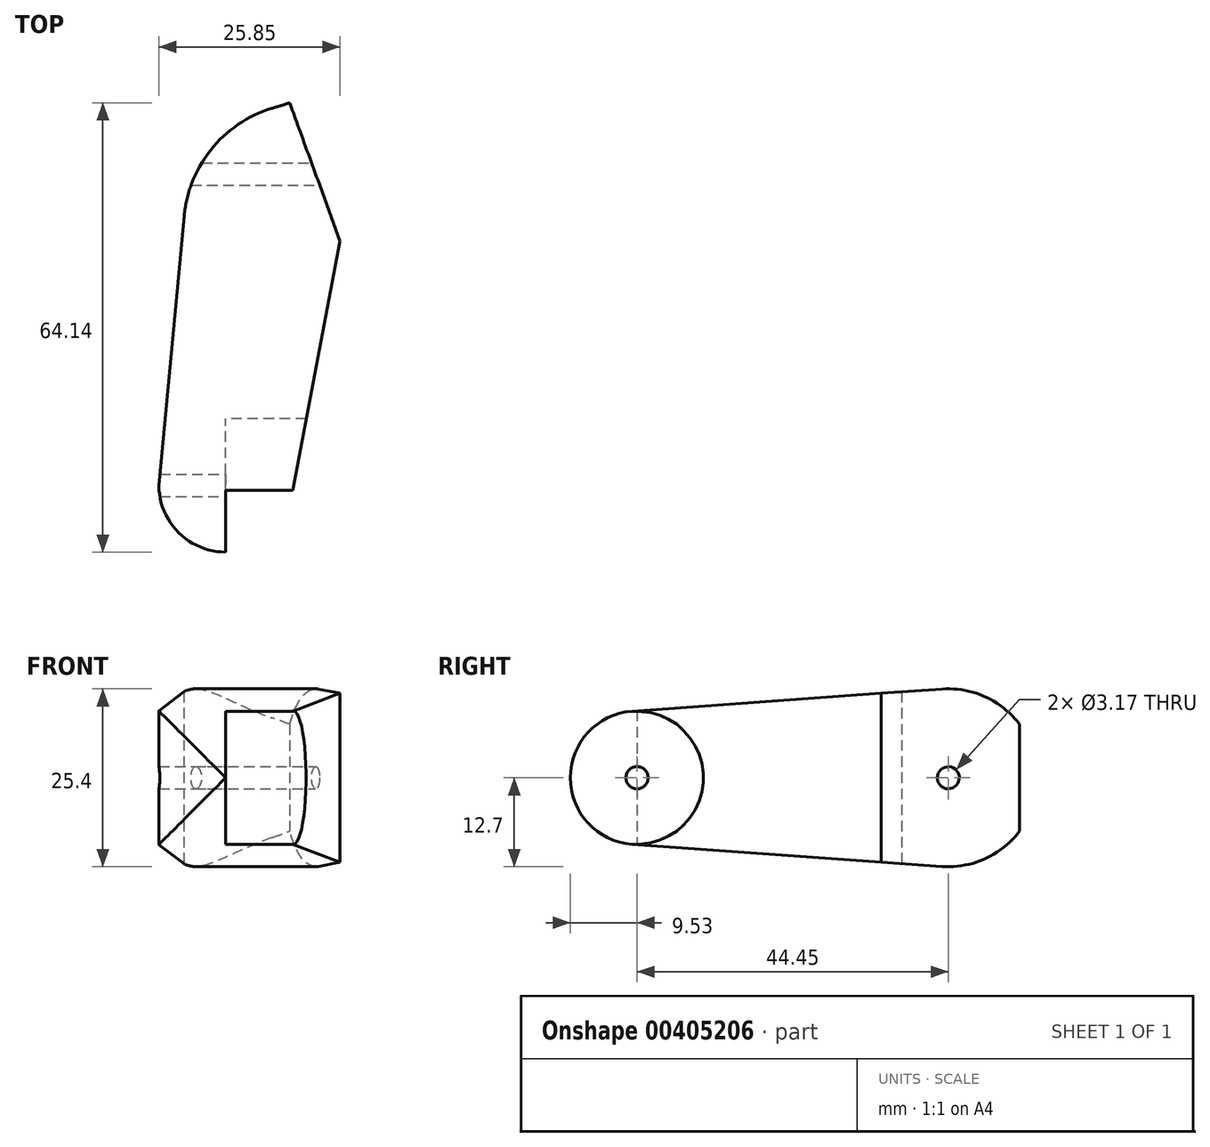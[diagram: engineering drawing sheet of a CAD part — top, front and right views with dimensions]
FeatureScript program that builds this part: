
annotation { "Feature Type Name" : "Feature", "Feature Type Description" : "" }
export const myFeature = defineFeature(function(context is Context, id is Id, definition is map)
    precondition{}
    {
        {
            var Q0;
            Q0=qCreatedBy(makeId("Top.planeOp"),FACE);
            var sketch = newSketch(context, id + "F0", { "sketchPlane" : qUnion([Q0])});
            skLineSegment(sketch, "E0", {"start": v(-24.07, -44.45) * mm, "end": v(33.85, -44.45) * mm, "construction": true});
            skLineSegment(sketch, "E1", {"start": v(-3.18, 19.25) * mm, "end": v(-3.17, -36.51) * mm, "construction": true});
            skLineSegment(sketch, "E2", {"start": v(13.15, -9.58) * mm, "end": v(6.1, -46.62) * mm});
            skPoint(sketch, "E3.middle", {"position": v(-3.17, -44.45) * mm});
            skLineSegment(sketch, "E4", {"start": v(0, 0) * mm, "end": v(-3.17, 0) * mm});
            skLineSegment(sketch, "E5", {"start": v(0, 0) * mm, "end": v(-36.28, 0) * mm});
            skPoint(sketch, "E5.endSnap0", {"position": v(-1.59, 0) * mm});
            skLineSegment(sketch, "E6.0", {"start": v(5.97, 10.16) * mm, "end": v(13.15, -9.58) * mm});
            skLineSegment(sketch, "E7", {"start": v(5.97, 10.16) * mm, "end": v(3.44, 9.4) * mm});
            skPoint(sketch, "E8.visualSharp", {"position": v(12.41, -13.45) * mm});
            skPoint(sketch, "E9.visualSharp", {"position": v(-8.5, 5.77) * mm});
            skArc(sketch, "E9.filletArc", {"start": v(3.44, 9.4) * mm, "mid": v(-5.4, 3.34) * mm, "end": v(-9.14, -6.69) * mm});
            skArc(sketch, "E10", {"start": v(-12.7, -44.45) * mm, "mid": v(-4.27, -53.91) * mm, "end": v(6.1, -46.62) * mm});
            skLineSegment(sketch, "E11", {"start": v(-9.14, -6.69) * mm, "end": v(-12.7, -44.45) * mm});
            skSolve(sketch);
        }
        {
            var Q0;
            Q0=qCreatedBy(makeId("Right.planeOp"),FACE);
            var sketch = newSketch(context, id + "F1", { "sketchPlane" : qUnion([Q0])});
            skArc(sketch, "E12", {"start": v(-0.9, -12.67) * mm, "mid": v(12.7, 0) * mm, "end": v(-0.9, 12.67) * mm});
            skArc(sketch, "E13", {"start": v(-45.13, 9.5) * mm, "mid": v(-53.98, 0) * mm, "end": v(-45.13, -9.5) * mm});
            skCircle(sketch, "E14", {"center": v(0, 0) * mm, "radius": 1.59 * mm});
            skCircle(sketch, "E15", {"center": v(-44.45, 0) * mm, "radius": 1.59 * mm});
            skLineSegment(sketch, "E16", {"start": v(-0.9, 12.67) * mm, "end": v(-45.13, 9.5) * mm});
            skLineSegment(sketch, "E17", {"start": v(-0.9, -12.67) * mm, "end": v(-45.13, -9.5) * mm});
            skSolve(sketch);
        }
        {
            var Q0;
            Q0=makeQuery(id+"F1.imprint","IMPRINT",FACE,{"disambiguationData":[TD([[makeQuery(id+"F1.imprint","IMPRINT",EDGE,{"derivedFrom":sQuery(id+"F1.wireOp",EDGE,"E12")}),1.0]])]});
            extrude(context, id + "F2", {"entities" : qUnion([Q0]), "endBound" : BoundingType.SYMMETRIC, "oppositeDirection" : true, "depth" : 50.8 * mm});
        }
        {
            var Q0;
            Q0=qSketchRegion(id+"F0",true);
            extrude(context, id + "F3", {"entities" : qUnion([Q0]), "operationType" : NewBodyOperationType.INTERSECT, "endBound" : BoundingType.SYMMETRIC, "depth" : 25.4 * mm});
        }
        {
            var Q0;
            Q0=qCreatedBy(makeId("Right.planeOp"),FACE);
            cPlane(context, id + "F4", {"entities" : qUnion([Q0]), "cplaneType" : CPlaneType.OFFSET, "offset" : 3.17 * mm, "oppositeDirection" : true, "width" : 152.4 * mm, "height" : 152.4 * mm});
        }
        {
            var Q0;
            Q0=qCreatedBy(id+"F4.planeOp",FACE);
            var sketch = newSketch(context, id + "F5", { "sketchPlane" : qUnion([Q0])});
            skCircle(sketch, "E18.0", {"center": v(-44.45, 0) * mm, "radius": 1.59 * mm});
            skCircle(sketch, "E19", {"center": v(-44.45, 0) * mm, "radius": 9.53 * mm});
            skSolve(sketch);
        }
        {
            var Q0;
            Q0 = qSketchRegion(id + "F5", true);
            extrude(context, id + "F6", {"entities" : qUnion([Q0]), "operationType" : NewBodyOperationType.REMOVE, "depth" : 25.4 * mm});
        }
    });
